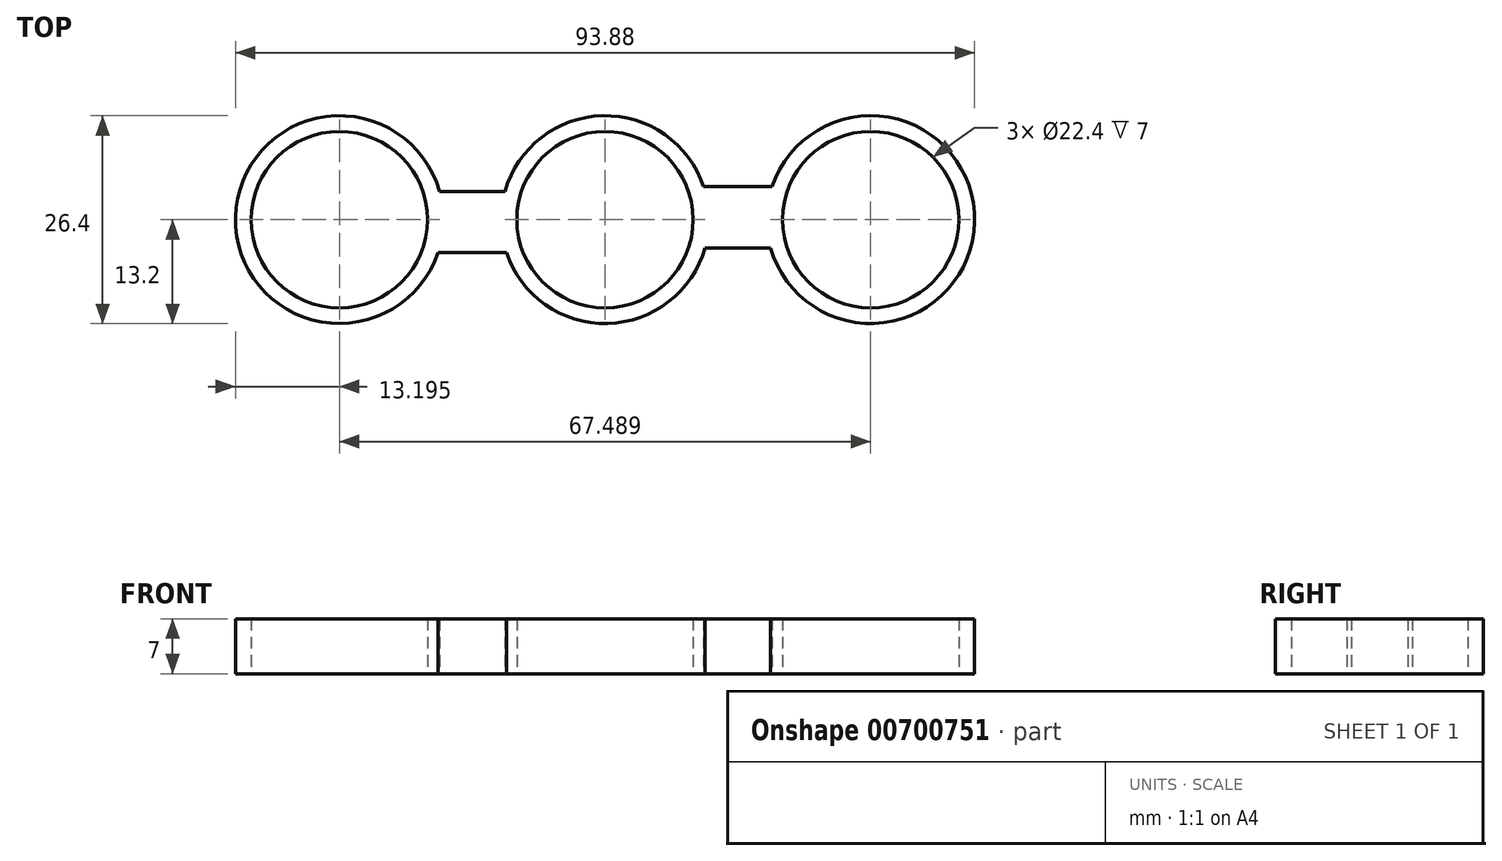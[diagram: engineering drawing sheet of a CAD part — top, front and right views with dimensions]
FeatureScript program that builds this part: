
annotation { "Feature Type Name" : "Feature", "Feature Type Description" : "" }
export const myFeature = defineFeature(function(context is Context, id is Id, definition is map)
    precondition{}
    {
        {
            var Q0;
            Q0=qCreatedBy(makeId("Top.planeOp"),FACE);
            var sketch = newSketch(context, id + "F0", { "sketchPlane" : qUnion([Q0])});
            skCircle(sketch, "E0", {"center": v(0, 0) * mm, "radius": 11.2 * mm});
            skArc(sketch, "E1", {"start": v(12.52, 4.17) * mm, "mid": v(-0.3, 13.2) * mm, "end": v(-12.7, 3.59) * mm});
            skCircle(sketch, "E2", {"center": v(-33.74, 0) * mm, "radius": 11.2 * mm});
            skArc(sketch, "E3", {"start": v(-21.04, 3.59) * mm, "mid": v(-46.94, 0.3) * mm, "end": v(-21.22, -4.17) * mm});
            skCircle(sketch, "E4.1.0", {"center": v(33.74, 0) * mm, "radius": 11.2 * mm});
            skArc(sketch, "E4.1.1", {"start": v(21.04, -3.59) * mm, "mid": v(46.94, -0.3) * mm, "end": v(21.22, 4.17) * mm});
            skLineSegment(sketch, "E5", {"start": v(-21.04, 3.59) * mm, "end": v(-12.7, 3.59) * mm});
            skLineSegment(sketch, "E6", {"start": v(-21.22, -4.17) * mm, "end": v(-12.52, -4.17) * mm});
            skLineSegment(sketch, "E7.1.0", {"start": v(21.04, -3.59) * mm, "end": v(12.7, -3.59) * mm});
            skLineSegment(sketch, "E7.1.1", {"start": v(21.22, 4.17) * mm, "end": v(12.52, 4.17) * mm});
            skArc(sketch, "E8.trimOffspring", {"start": v(-12.52, -4.17) * mm, "mid": v(0.3, -13.2) * mm, "end": v(12.7, -3.59) * mm});
            skSolve(sketch);
        }
        {
            var Q0;
            Q0=makeQuery(id+"F0.imprint","IMPRINT",FACE,{"disambiguationData":[TD([[makeQuery(id+"F0.imprint","IMPRINT",EDGE,{"derivedFrom":sQuery(id+"F0.wireOp",EDGE,"E0")}),-1.0]])]});
            extrude(context, id + "F1", {"entities" : qUnion([Q0]), "depth" : 7 * mm, "offsetDistance" : 25 * mm});
        }
    });
